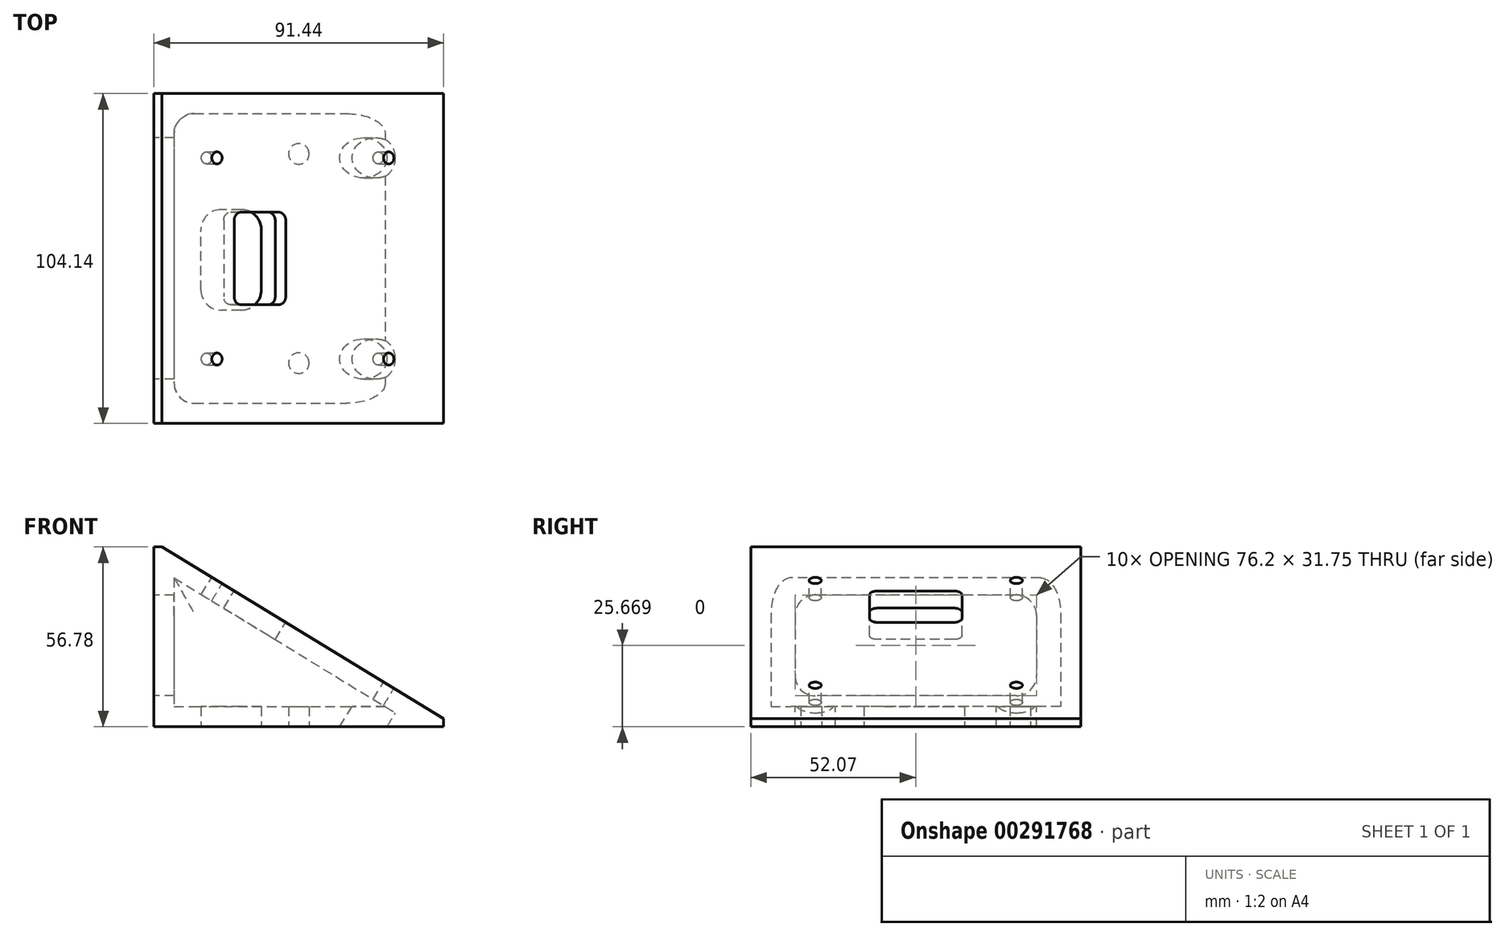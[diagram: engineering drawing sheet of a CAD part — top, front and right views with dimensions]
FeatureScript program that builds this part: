
annotation { "Feature Type Name" : "Feature", "Feature Type Description" : "" }
export const myFeature = defineFeature(function(context is Context, id is Id, definition is map)
    precondition{}
    {
        {
            var Q0;
            Q0=qCreatedBy(makeId("Front.planeOp"),FACE);
            var sketch = newSketch(context, id + "F0", { "sketchPlane" : qUnion([Q0])});
            skLineSegment(sketch, "E0.bottom", {"start": v(-39.73, 56.6) * mm, "end": v(-37.2, 56.6) * mm});
            skLineSegment(sketch, "E0.top", {"start": v(-39.73, -0.19) * mm, "end": v(51.7, -0.19) * mm});
            skLineSegment(sketch, "E0.left", {"start": v(-39.73, 56.6) * mm, "end": v(-39.73, -0.19) * mm});
            skLineSegment(sketch, "E0.right", {"start": v(51.7, 2.35) * mm, "end": v(51.7, -0.19) * mm});
            skLineSegment(sketch, "E1", {"start": v(-37.2, 56.6) * mm, "end": v(51.7, 2.35) * mm});
            skLineSegment(sketch, "E2", {"start": v(-39.73, 56.6) * mm, "end": v(-37.2, 56.6) * mm, "construction": true});
            skLineSegment(sketch, "E3", {"start": v(51.7, 2.35) * mm, "end": v(51.7, -0.19) * mm, "construction": true});
            skSolve(sketch);
        }
        {
            var Q0;
            Q0 = qSketchRegion(id + "F0", true);
            extrude(context, id + "F1", {"entities" : qUnion([Q0]), "oppositeDirection" : true, "depth" : 104.14 * mm});
        }
        {
            var Q0;
            Q0=makeQuery(id+"F1.opExtrude","SWEPT_FACE",FACE,{"disambiguationData":[OSD([sQuery(id+"F0.wireOp",EDGE,"E1")])]});
            var Q1;
            Q1=makeQuery(id+"F1.opExtrude","SWEPT_BODY",BODY,{"disambiguationData":[OSD([sQuery(id+"F0.wireOp",EDGE,"E0.bottom"),sQuery(id+"F0.wireOp",EDGE,"E0.top"),sQuery(id+"F0.wireOp",EDGE,"E0.left"),sQuery(id+"F0.wireOp",EDGE,"E0.right"),sQuery(id+"F0.wireOp",EDGE,"E1")])]});
            shell(context, id + "F2", {"isHollow" : true, "entities" : qUnion([Q0]), "parts" : qUnion([Q1]), "thickness" : 6.35 * mm});
        }
        {
            var Q0;
            Q0=makeQuery(id+"F1.opExtrude","SWEPT_FACE",FACE,{"disambiguationData":[OSD([sQuery(id+"F0.wireOp",EDGE,"E1")])]});
            var sketch = newSketch(context, id + "F3", { "sketchPlane" : qUnion([Q0])});
            skLineSegment(sketch, "E4.bottom", {"start": v(-40.9, 20.32) * mm, "end": v(22.6, 20.32) * mm, "construction": true});
            skLineSegment(sketch, "E4.top", {"start": v(-40.9, 83.82) * mm, "end": v(22.6, 83.82) * mm, "construction": true});
            skLineSegment(sketch, "E4.left", {"start": v(-40.9, 20.32) * mm, "end": v(-40.9, 83.82) * mm, "construction": true});
            skLineSegment(sketch, "E4.right", {"start": v(22.6, 20.32) * mm, "end": v(22.6, 83.82) * mm, "construction": true});
            skLineSegment(sketch, "E5", {"start": v(-9.16, 20.32) * mm, "end": v(-9.16, 0) * mm, "construction": true});
            skPoint(sketch, "E5.startSnap0", {"position": v(-9.16, 0) * mm});
            skLineSegment(sketch, "E6", {"start": v(-9.16, 83.82) * mm, "end": v(-9.16, 104.14) * mm, "construction": true});
            skLineSegment(sketch, "E7", {"start": v(-40.9, 52.07) * mm, "end": v(-61.23, 52.07) * mm, "construction": true});
            skLineSegment(sketch, "E8", {"start": v(22.6, 52.07) * mm, "end": v(42.91, 52.07) * mm, "construction": true});
            skCircle(sketch, "E9", {"center": v(22.6, 83.82) * mm, "radius": 6.35 * mm});
            skCircle(sketch, "E10", {"center": v(22.6, 20.32) * mm, "radius": 6.35 * mm});
            skSolve(sketch);
        }
        {
            var Q0;
            Q0=sQuery(id+"F3.wireOp",VERTEX,"E4.bottom.start");
            var Q1;
            Q1=sQuery(id+"F3.wireOp",VERTEX,"E4.left.end");
            var Q2;
            Q2=sQuery(id+"F3.wireOp",VERTEX,"E4.right.end");
            var Q3;
            Q3=sQuery(id+"F3.wireOp",VERTEX,"E4.right.start");
            var Q4;
            Q4=makeQuery(id+"F1.opExtrude","SWEPT_BODY",BODY,{"disambiguationData":[OSD([sQuery(id+"F0.wireOp",EDGE,"E0.bottom"),sQuery(id+"F0.wireOp",EDGE,"E0.top"),sQuery(id+"F0.wireOp",EDGE,"E0.left"),sQuery(id+"F0.wireOp",EDGE,"E0.right"),sQuery(id+"F0.wireOp",EDGE,"E1")])]});
            hole(context, id + "F4", {"style" : HoleStyle.SIMPLE, "endStyle" : HoleEndStyle.BLIND, "holeDiameter" : 3.8 * mm, "holeDepth" : 6.6 * mm, "tappedDepth" : 12.7 * mm, "tapClearance" : 3, "locations" : qUnion([Q0, Q1, Q2, Q3]), "scope" : qUnion([Q4])});
        }
        {
            var Q0;
            Q0=makeQuery(id+"F1.opExtrude","SWEPT_FACE",FACE,{"disambiguationData":[OSD([sQuery(id+"F0.wireOp",EDGE,"E1")])]});
            var sketch = newSketch(context, id + "F5", { "sketchPlane" : qUnion([Q0])});
            skLineSegment(sketch, "E11.bottom", {"start": v(-32.02, 37.46) * mm, "end": v(-18.05, 37.46) * mm});
            skLineSegment(sketch, "E11.top", {"start": v(-32.02, 66.67) * mm, "end": v(-18.05, 66.67) * mm});
            skLineSegment(sketch, "E11.left", {"start": v(-34.56, 40) * mm, "end": v(-34.56, 64.13) * mm});
            skLineSegment(sketch, "E11.right", {"start": v(-15.5, 40) * mm, "end": v(-15.5, 64.13) * mm});
            skLineSegment(sketch, "E12", {"start": v(-25.03, 66.67) * mm, "end": v(-25.03, 104.14) * mm, "construction": true});
            skLineSegment(sketch, "E13", {"start": v(22.6, 20.32) * mm, "end": v(22.6, 83.82) * mm, "construction": true});
            skPoint(sketch, "E14.visualSharp", {"position": v(-34.56, 66.67) * mm});
            skArc(sketch, "E14.filletArc", {"start": v(-32.02, 66.67) * mm, "mid": v(-33.81, 65.93) * mm, "end": v(-34.56, 64.13) * mm});
            skPoint(sketch, "E15.visualSharp", {"position": v(-15.5, 66.67) * mm});
            skArc(sketch, "E15.filletArc", {"start": v(-15.5, 64.13) * mm, "mid": v(-16.25, 65.93) * mm, "end": v(-18.05, 66.67) * mm});
            skPoint(sketch, "E16.visualSharp", {"position": v(-15.5, 37.46) * mm});
            skArc(sketch, "E16.filletArc", {"start": v(-18.05, 37.46) * mm, "mid": v(-16.25, 38.2) * mm, "end": v(-15.5, 40) * mm});
            skPoint(sketch, "E17.visualSharp", {"position": v(-34.56, 37.46) * mm});
            skArc(sketch, "E17.filletArc", {"start": v(-34.56, 40) * mm, "mid": v(-33.81, 38.2) * mm, "end": v(-32.02, 37.46) * mm});
            skLineSegment(sketch, "E18", {"start": v(-40.9, 83.82) * mm, "end": v(-40.9, 20.32) * mm, "construction": true});
            skSolve(sketch);
        }
        {
            var Q0;
            Q0 = qSketchRegion(id + "F5", true);
            extrude(context, id + "F6", {"entities" : qUnion([Q0]), "operationType" : NewBodyOperationType.REMOVE, "oppositeDirection" : true, "depth" : 12.7 * mm});
        }
        {
            var Q0;
            Q0=makeQuery(id+"F1.opExtrude","SWEPT_FACE",FACE,{"disambiguationData":[OSD([sQuery(id+"F0.wireOp",EDGE,"E0.left")])]});
            var sketch = newSketch(context, id + "F7", { "sketchPlane" : qUnion([Q0])});
            skLineSegment(sketch, "E19.bottom", {"start": v(-83.82, 41.35) * mm, "end": v(-20.32, 41.35) * mm});
            skLineSegment(sketch, "E19.top", {"start": v(-83.82, 9.6) * mm, "end": v(-20.32, 9.6) * mm});
            skLineSegment(sketch, "E19.left", {"start": v(-90.17, 35) * mm, "end": v(-90.17, 15.95) * mm});
            skLineSegment(sketch, "E19.right", {"start": v(-13.97, 35) * mm, "end": v(-13.97, 15.95) * mm});
            skPoint(sketch, "E20.visualSharp", {"position": v(-13.97, 41.35) * mm});
            skArc(sketch, "E20.filletArc", {"start": v(-13.97, 35) * mm, "mid": v(-15.83, 39.5) * mm, "end": v(-20.32, 41.35) * mm});
            skPoint(sketch, "E21.visualSharp", {"position": v(-13.97, 9.6) * mm});
            skArc(sketch, "E21.filletArc", {"start": v(-20.32, 9.6) * mm, "mid": v(-15.83, 11.46) * mm, "end": v(-13.97, 15.95) * mm});
            skPoint(sketch, "E22.visualSharp", {"position": v(-90.17, 9.6) * mm});
            skArc(sketch, "E22.filletArc", {"start": v(-90.17, 15.95) * mm, "mid": v(-88.31, 11.46) * mm, "end": v(-83.82, 9.6) * mm});
            skPoint(sketch, "E23.visualSharp", {"position": v(-90.17, 41.35) * mm});
            skArc(sketch, "E23.filletArc", {"start": v(-83.82, 41.35) * mm, "mid": v(-88.31, 39.5) * mm, "end": v(-90.17, 35) * mm});
            skLineSegment(sketch, "E24", {"start": v(-90.17, 25.48) * mm, "end": v(-104.14, 25.48) * mm, "construction": true});
            skLineSegment(sketch, "E25", {"start": v(-13.97, 28.2) * mm, "end": v(0, 28.2) * mm, "construction": true});
            skPoint(sketch, "E25.startSnap0", {"position": v(-104.14, 28.2) * mm});
            skLineSegment(sketch, "E26", {"start": v(-52.07, 9.6) * mm, "end": v(-52.07, -0.19) * mm, "construction": true});
            skLineSegment(sketch, "E27", {"start": v(-52.07, 41.35) * mm, "end": v(-52.07, 56.6) * mm, "construction": true});
            skSolve(sketch);
        }
        {
            var Q0;
            Q0 = qSketchRegion(id + "F7", true);
            extrude(context, id + "F8", {"entities" : qUnion([Q0]), "operationType" : NewBodyOperationType.REMOVE, "oppositeDirection" : true, "depth" : 12.7 * mm});
        }
        {
            var Q0;
            Q0=makeQuery(id+"F2.opShell","OFFSET_EDGE",EDGE,{"disambiguationData":[OSD([sQuery(id+"F0.wireOp",EDGE,"E0.right"),sQuery(id+"F0.wireOp",EDGE,"E1")])]});
            var Q1;
            Q1=makeQuery(id+"F2.opShell","OFFSET_EDGE",EDGE,{"disambiguationData":[OSD([sQuery(id+"F0.wireOp",EDGE,"E0.bottom"),sQuery(id+"F0.wireOp",EDGE,"E1")])]});
            var Q2;
            {var subQ0=sQuery(id+"F0.wireOp",EDGE,"E1");Q2=makeQuery(id+"F2.opShell","OFFSET_EDGE",EDGE,{"disambiguationData":[OSD([subQ0]),TDD([makeQuery(id+"F1.opExtrude","CAP_EDGE",EDGE,{"disambiguationData":[OSD([subQ0])],"isStart":true})])]});}
            var Q3;
            {var subQ0=sQuery(id+"F0.wireOp",EDGE,"E1");Q3=makeQuery(id+"F2.opShell","OFFSET_EDGE",EDGE,{"disambiguationData":[OSD([subQ0]),TDD([makeQuery(id+"F1.opExtrude","CAP_EDGE",EDGE,{"disambiguationData":[OSD([subQ0])],"isStart":false})])]});}
            var Q4;
            {var subQ0=sQuery(id+"F0.wireOp",EDGE,"E0.left");Q4=makeQuery(id+"F2.opShell","OFFSET_EDGE",EDGE,{"disambiguationData":[OSD([subQ0]),TDD([makeQuery(id+"F1.opExtrude","CAP_EDGE",EDGE,{"disambiguationData":[OSD([subQ0])],"isStart":true})])]});}
            var Q5;
            {var subQ0=sQuery(id+"F0.wireOp",EDGE,"E0.left");Q5=makeQuery(id+"F2.opShell","OFFSET_EDGE",EDGE,{"disambiguationData":[OSD([subQ0]),TDD([makeQuery(id+"F1.opExtrude","CAP_EDGE",EDGE,{"disambiguationData":[OSD([subQ0])],"isStart":false})])]});}
            fillet(context, id + "F9", {"entities" : qUnion([Q0, Q1, Q2, Q3, Q4, Q5]), "radius" : 6.35 * mm, "tangentPropagation" : true, "allowEdgeOverflow" : false});
        }
        {
            var Q0;
            Q0=makeQuery(id+"F3.imprint","IMPRINT",FACE,{"disambiguationData":[TD([[makeQuery(id+"F3.imprint","IMPRINT",EDGE,{"derivedFrom":sQuery(id+"F3.wireOp",EDGE,"E9")}),1.0]])]});
            var Q1;
            Q1=makeQuery(id+"F3.imprint","IMPRINT",FACE,{"disambiguationData":[TD([[makeQuery(id+"F3.imprint","IMPRINT",EDGE,{"derivedFrom":sQuery(id+"F3.wireOp",EDGE,"E10")}),1.0]])]});
            extrude(context, id + "F10", {"entities" : qUnion([Q0, Q1]), "operationType" : NewBodyOperationType.REMOVE, "oppositeDirection" : true, "depth" : 25.4 * mm, "hasSecondDirection" : true, "secondDirectionOppositeDirection" : true, "secondDirectionDepth" : 6.35 * mm});
        }
        {
            var Q0;
            Q0=makeQuery(id+"F1.opExtrude","SWEPT_FACE",FACE,{"disambiguationData":[OSD([sQuery(id+"F0.wireOp",EDGE,"E0.top")])]});
            var sketch = newSketch(context, id + "F11", { "sketchPlane" : qUnion([Q0])});
            skPoint(sketch, "E28", {"position": v(5.99, -19.05) * mm});
            skPoint(sketch, "E29", {"position": v(5.99, -85.1) * mm});
            skLineSegment(sketch, "E30.bottom", {"start": v(-12.2, -35.77) * mm, "end": v(-18.56, -35.77) * mm});
            skLineSegment(sketch, "E30.top", {"start": v(-12.2, -67.52) * mm, "end": v(-18.56, -67.52) * mm});
            skLineSegment(sketch, "E30.left", {"start": v(-5.86, -42.12) * mm, "end": v(-5.86, -61.17) * mm});
            skLineSegment(sketch, "E30.right", {"start": v(-24.9, -42.12) * mm, "end": v(-24.9, -61.17) * mm});
            skPoint(sketch, "E31.visualSharp", {"position": v(-5.86, -35.77) * mm});
            skArc(sketch, "E31.filletArc", {"start": v(-5.86, -42.12) * mm, "mid": v(-7.72, -37.63) * mm, "end": v(-12.2, -35.77) * mm});
            skPoint(sketch, "E32.visualSharp", {"position": v(-24.9, -35.77) * mm});
            skArc(sketch, "E32.filletArc", {"start": v(-18.56, -35.77) * mm, "mid": v(-23.05, -37.63) * mm, "end": v(-24.9, -42.12) * mm});
            skPoint(sketch, "E33.visualSharp", {"position": v(-24.9, -67.52) * mm});
            skArc(sketch, "E33.filletArc", {"start": v(-24.9, -61.17) * mm, "mid": v(-23.05, -65.66) * mm, "end": v(-18.56, -67.52) * mm});
            skPoint(sketch, "E34.visualSharp", {"position": v(-5.86, -67.52) * mm});
            skArc(sketch, "E34.filletArc", {"start": v(-12.2, -67.52) * mm, "mid": v(-7.72, -65.66) * mm, "end": v(-5.86, -61.17) * mm});
            skSolve(sketch);
        }
        {
            var Q0;
            Q0=makeQuery(id+"F11.imprint","IMPRINT",FACE,{"disambiguationData":[TD([[makeQuery(id+"F11.imprint","IMPRINT",EDGE,{"derivedFrom":sQuery(id+"F11.wireOp",EDGE,"E30.bottom")}),1.0]])]});
            extrude(context, id + "F12", {"entities" : qUnion([Q0]), "operationType" : NewBodyOperationType.REMOVE, "oppositeDirection" : true, "depth" : 6.35 * mm});
        }
        {
            var Q0;
            Q0=sQuery(id+"F11.wireOp",VERTEX,"E28");
            var Q1;
            Q1=sQuery(id+"F11.wireOp",VERTEX,"E29");
            var Q2;
            Q2=makeQuery(id+"F1.opExtrude","SWEPT_BODY",BODY,{"disambiguationData":[OSD([sQuery(id+"F0.wireOp",EDGE,"E0.bottom"),sQuery(id+"F0.wireOp",EDGE,"E0.top"),sQuery(id+"F0.wireOp",EDGE,"E0.left"),sQuery(id+"F0.wireOp",EDGE,"E0.right"),sQuery(id+"F0.wireOp",EDGE,"E1")])]});
            hole(context, id + "F13", {"style" : HoleStyle.SIMPLE, "endStyle" : HoleEndStyle.BLIND, "standardTappedOrClearance" : lookupTablePath({ "standard" : "ANSI", "fit" : "Close", "size" : "1/4", "type" : "Clearance" }), "standardBlindInLast" : lookupTablePath({ "fit" : "Close", "standard" : "ANSI", "size" : "1/4", "type" : "Clearance" }), "holeDiameter" : 6.53 * mm, "holeDepth" : 6.6 * mm, "tappedDepth" : 12.7 * mm, "tapClearance" : 3, "locations" : qUnion([Q0, Q1]), "scope" : qUnion([Q2])});
        }
    });
